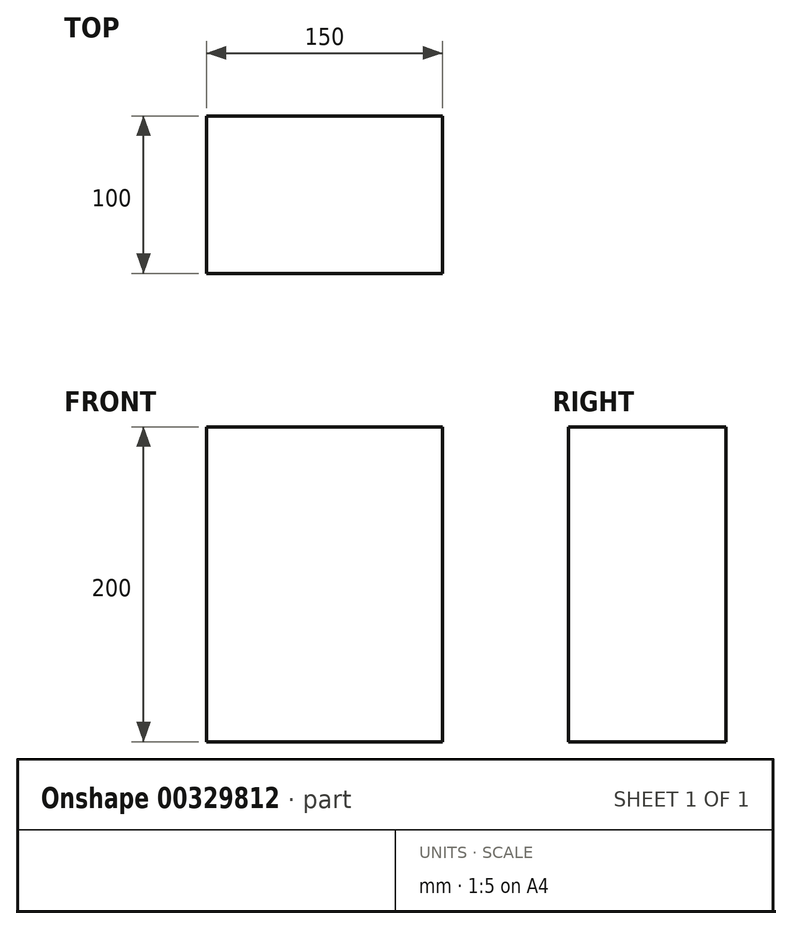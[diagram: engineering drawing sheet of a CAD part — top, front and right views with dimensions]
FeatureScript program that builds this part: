
annotation { "Feature Type Name" : "Feature", "Feature Type Description" : "" }
export const myFeature = defineFeature(function(context is Context, id is Id, definition is map)
    precondition{}
    {
        {
            var Q0;
            Q0=qCreatedBy(makeId("Top.planeOp"),FACE);
            var sketch = newSketch(context, id + "F0", { "sketchPlane" : qUnion([Q0])});
            skLineSegment(sketch, "E0.bottom", {"start": v(-72.09, 50.87) * mm, "end": v(77.91, 50.87) * mm});
            skLineSegment(sketch, "E0.top", {"start": v(-72.09, -49.13) * mm, "end": v(77.91, -49.13) * mm});
            skLineSegment(sketch, "E0.left", {"start": v(-72.09, 50.87) * mm, "end": v(-72.09, -49.13) * mm});
            skLineSegment(sketch, "E0.right", {"start": v(77.91, 50.87) * mm, "end": v(77.91, -49.13) * mm});
            skSolve(sketch);
        }
        {
            var Q0;
            Q0=makeQuery(id+"F0.imprint","IMPRINT",FACE,{"disambiguationData":[TD([[makeQuery(id+"F0.imprint","IMPRINT",EDGE,{"derivedFrom":sQuery(id+"F0.wireOp",EDGE,"E0.bottom")}),-1.0]])]});
            extrude(context, id + "F1", {"entities" : qUnion([Q0]), "depth" : 200 * mm});
        }
    });
